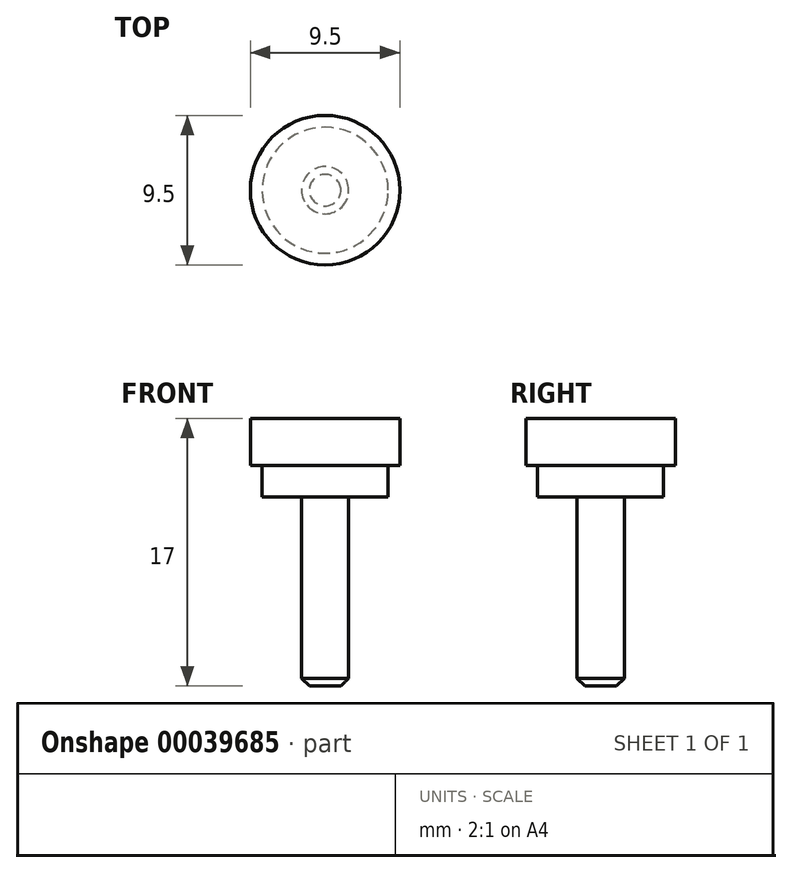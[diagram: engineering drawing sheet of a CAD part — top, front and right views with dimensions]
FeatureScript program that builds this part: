
annotation { "Feature Type Name" : "Feature", "Feature Type Description" : "" }
export const myFeature = defineFeature(function(context is Context, id is Id, definition is map)
    precondition{}
    {
        {
            var Q0;
            Q0=qCreatedBy(makeId("Front.planeOp"),FACE);
            var sketch = newSketch(context, id + "F0", { "sketchPlane" : qUnion([Q0])});
            skLineSegment(sketch, "E0", {"start": v(-4.75, 0) * mm, "end": v(-4.75, -3) * mm});
            skLineSegment(sketch, "E1", {"start": v(-4.75, -3) * mm, "end": v(-4, -3) * mm});
            skLineSegment(sketch, "E2", {"start": v(-4, -3) * mm, "end": v(-4, -5) * mm});
            skLineSegment(sketch, "E3", {"start": v(-4, -5) * mm, "end": v(-1.5, -5) * mm});
            skLineSegment(sketch, "E4", {"start": v(-1.5, -5) * mm, "end": v(-1.5, -17) * mm});
            skLineSegment(sketch, "E5", {"start": v(-1.5, -17) * mm, "end": v(0, -17) * mm});
            skLineSegment(sketch, "E6", {"start": v(0, -17) * mm, "end": v(0, 0) * mm});
            skLineSegment(sketch, "E7", {"start": v(-4.75, 0) * mm, "end": v(0, 0) * mm});
            skSolve(sketch);
        }
        {
            var Q0;
            Q0=makeQuery(id+"F0.imprint","IMPRINT",FACE,{"disambiguationData":[TD([[makeQuery(id+"F0.imprint","IMPRINT",EDGE,{"derivedFrom":sQuery(id+"F0.wireOp",EDGE,"E0")}),1.0]])]});
            var Q1;
            Q1=sQuery(id+"F0.wireOp",EDGE,"E6");
            revolve(context, id + "F1", {"entities" : qUnion([Q0]), "axis" : qUnion([Q1]), "revolveType" : RevolveType.FULL});
        }
        {
            var Q0;
            Q0=makeQuery(id+"F1.opRevolve","SWEPT_EDGE",EDGE,{"disambiguationData":[OSD([sQuery(id+"F0.wireOp",EDGE,"E4"),sQuery(id+"F0.wireOp",EDGE,"E5")])]});
            chamfer(context, id + "F2", {"entities" : qUnion([Q0]), "width" : 0.5 * mm, "tangentPropagation" : true});
        }
    });
